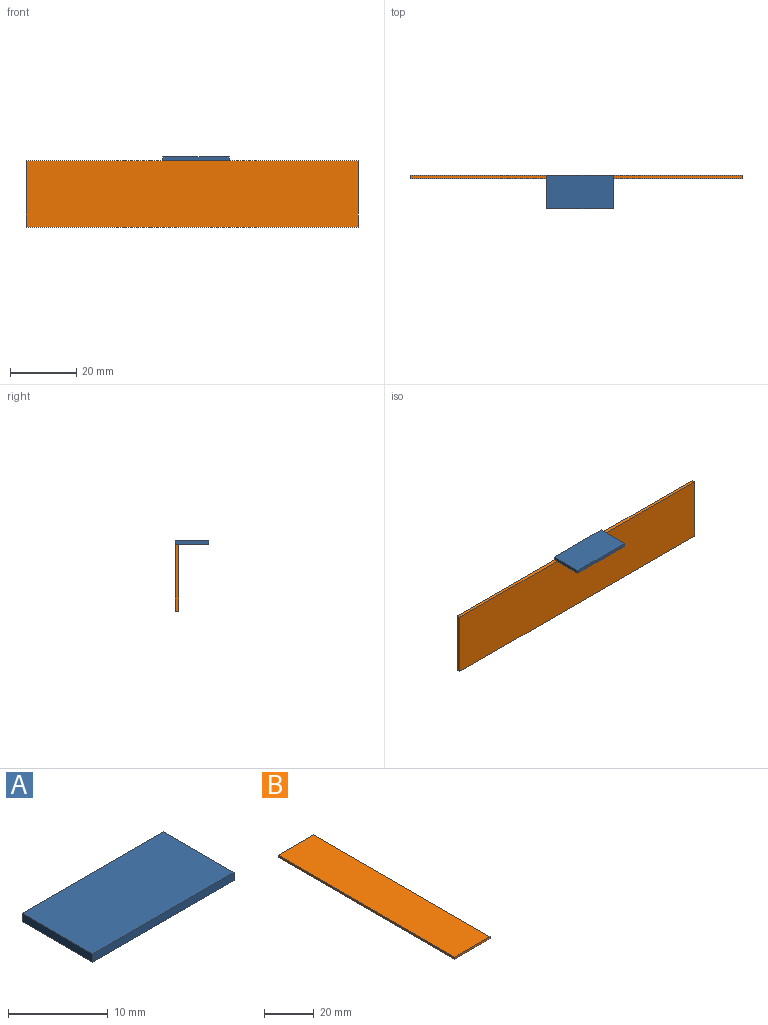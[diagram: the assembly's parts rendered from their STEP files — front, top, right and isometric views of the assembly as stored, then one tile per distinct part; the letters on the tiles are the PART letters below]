
ASSEMBLY  parts=2 mates=2
PART A: 6 faces, bbox 20x10x1 mm
  f0: plane 20x1mm, normal (0,1,0), area 20mm2, adj f1,f3,f4,f5
  f1: plane 10x1mm, normal (-1,0,0), area 10mm2, adj f0,f2,f4,f5
  f2: plane 20x1mm, normal (0,-1,0), area 20mm2, adj f1,f3,f4,f5
  f3: plane 10x1mm, normal (1,0,0), area 10mm2, adj f0,f2,f4,f5
  f4: plane 20x10mm, normal (0,0,1), area 200mm2, adj f0,f1,f2,f3
  f5: plane 20x10mm, normal (0,0,-1), area 200mm2, adj f0,f1,f2,f3
PART B: 6 faces, bbox 20x100x1 mm
  f0: plane 20x1mm, normal (0,1,0), area 20mm2, adj f1,f3,f4,f5
  f1: plane 100x1mm, normal (-1,0,0), area 100mm2, adj f0,f2,f4,f5
  f2: plane 20x1mm, normal (0,-1,0), area 20mm2, adj f1,f3,f4,f5
  f3: plane 100x1mm, normal (1,0,0), area 100mm2, adj f0,f2,f4,f5
  f4: plane 100x20mm, normal (0,0,1), area 2000mm2, adj f0,f1,f2,f3
  f5: plane 100x20mm, normal (0,0,-1), area 2000mm2, adj f0,f1,f2,f3
PLACE A t=(-3.95,8.3,5.88)mm
PLACE B rot(axis=(-0.58,0.58,0.58),120deg) t=(-45.15,7.3,5.75)mm
MATE planar B.f4 <-> A.f0  axis (0,1,0) through (4.85,8.3,-4.25)mm
MATE parallel B.f3 <-> A.f4  axis (0,0,-1) through (4.85,7.8,-14.25)mm
